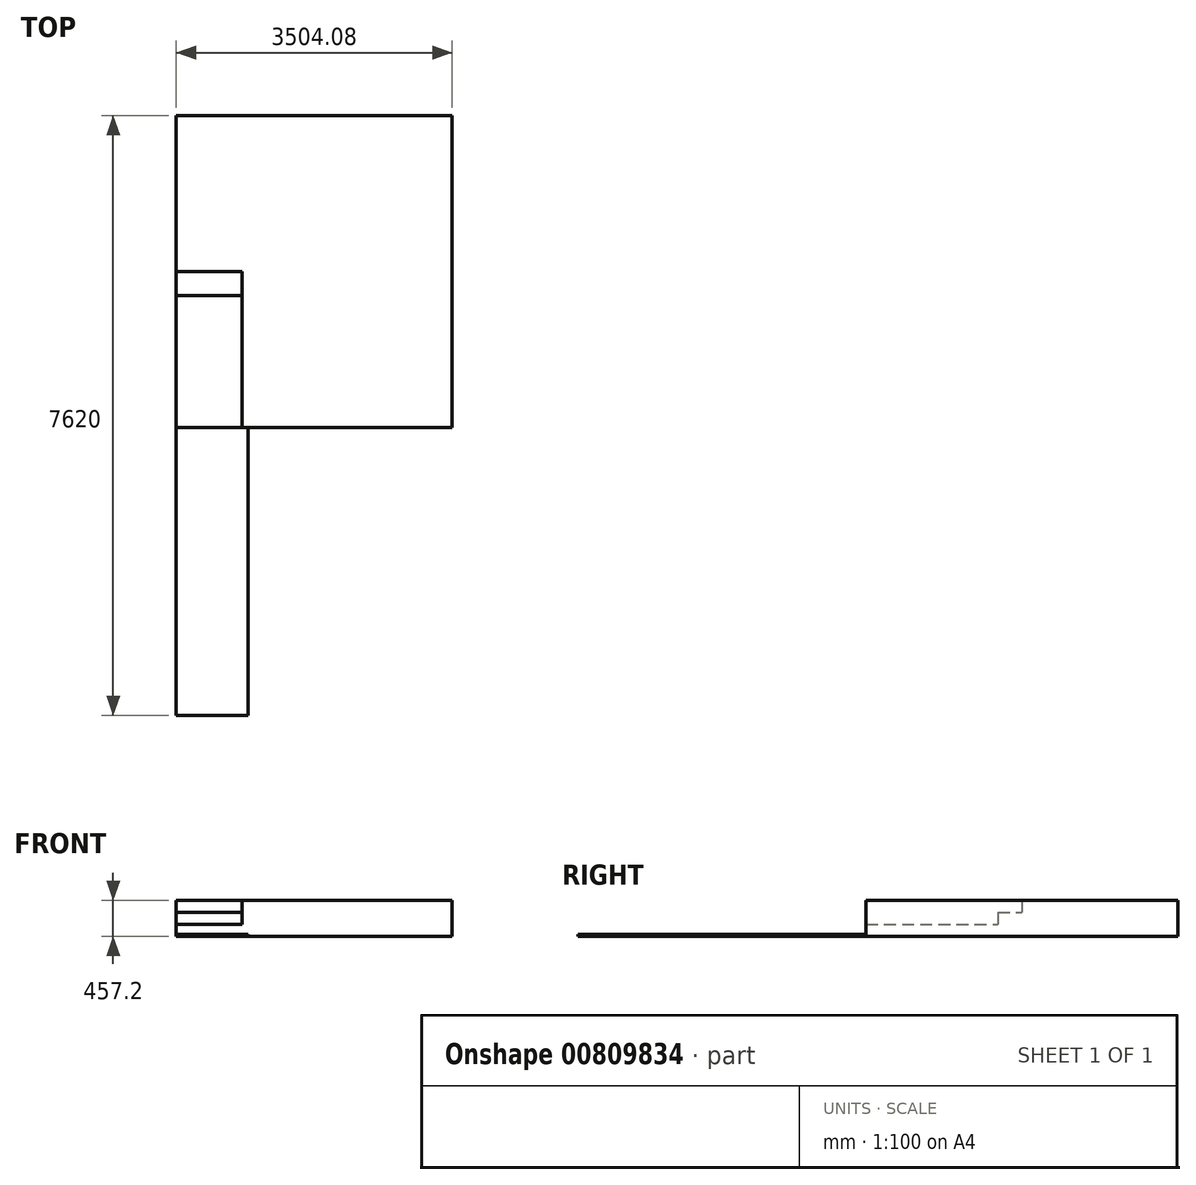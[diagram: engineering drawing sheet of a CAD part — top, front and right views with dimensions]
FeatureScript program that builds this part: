
annotation { "Feature Type Name" : "Feature", "Feature Type Description" : "" }
export const myFeature = defineFeature(function(context is Context, id is Id, definition is map)
    precondition{}
    {
        {
            var Q0;
            Q0=qCreatedBy(makeId("Top.planeOp"),FACE);
            var sketch = newSketch(context, id + "F0", { "sketchPlane" : qUnion([Q0])});
            skLineSegment(sketch, "E0.bottom", {"start": v(1752.04, -1981.2) * mm, "end": v(-1752.04, -1981.2) * mm});
            skLineSegment(sketch, "E0.top", {"start": v(1752.04, 1981.2) * mm, "end": v(-1752.04, 1981.2) * mm});
            skLineSegment(sketch, "E0.left", {"start": v(1752.04, -1981.2) * mm, "end": v(1752.04, 1981.2) * mm});
            skLineSegment(sketch, "E0.right", {"start": v(-1752.04, -1981.2) * mm, "end": v(-1752.04, 1981.2) * mm});
            skPoint(sketch, "E0.middle", {"position": v(0, 0) * mm});
            skLineSegment(sketch, "E1.bottom", {"start": v(-1752.04, -1981.2) * mm, "end": v(-837.64, -1981.2) * mm});
            skLineSegment(sketch, "E1.top", {"start": v(-1752.04, -5638.8) * mm, "end": v(-837.64, -5638.8) * mm});
            skLineSegment(sketch, "E1.left", {"start": v(-1752.04, -1981.2) * mm, "end": v(-1752.04, -5638.8) * mm});
            skLineSegment(sketch, "E1.right", {"start": v(-837.64, -1981.2) * mm, "end": v(-837.64, -5638.8) * mm});
            skLineSegment(sketch, "E2.bottom", {"start": v(-1752.04, -1981.2) * mm, "end": v(-914.4, -1981.2) * mm});
            skLineSegment(sketch, "E2.top", {"start": v(-1752.04, -304.8) * mm, "end": v(-914.4, -304.8) * mm});
            skLineSegment(sketch, "E2.left", {"start": v(-1752.04, -1981.2) * mm, "end": v(-1752.04, -304.8) * mm});
            skLineSegment(sketch, "E2.right", {"start": v(-914.4, -1981.2) * mm, "end": v(-914.4, -304.8) * mm});
            skLineSegment(sketch, "E3.top", {"start": v(-1752.04, 0) * mm, "end": v(-914.4, 0) * mm});
            skLineSegment(sketch, "E3.left", {"start": v(-1752.04, -304.8) * mm, "end": v(-1752.04, 0) * mm});
            skLineSegment(sketch, "E3.right", {"start": v(-914.4, -304.8) * mm, "end": v(-914.4, 0) * mm});
            skSolve(sketch);
        }
        {
            var Q0;
            {var subQ4=sQuery(id+"F0.wireOp",EDGE,"E2.top");Q0=makeQuery(id+"F0.imprint","IMPRINT",FACE,{"disambiguationData":[TD([[makeQuery(id+"F0.imprint","IMPRINT",EDGE,{"derivedFrom":subQ4}),-1.0]])]});}
            extrude(context, id + "F1", {"entities" : qUnion([Q0]), "depth" : 152.4 * mm, "offsetDistance" : 25.4 * mm});
        }
        {
            var Q0;
            {var subQ2=sQuery(id+"F0.wireOp",EDGE,"E2.top");Q0=makeQuery(id+"F0.imprint","IMPRINT",FACE,{"disambiguationData":[TD([[makeQuery(id+"F0.imprint","IMPRINT",EDGE,{"derivedFrom":subQ2}),1.0]])]});}
            extrude(context, id + "F2", {"entities" : qUnion([Q0]), "operationType" : NewBodyOperationType.ADD, "depth" : 304.8 * mm, "offsetDistance" : 25.4 * mm});
        }
        {
            var Q0;
            {var subQ1=sQuery(id+"F0.wireOp",EDGE,"E0.top");Q0=makeQuery(id+"F0.imprint","IMPRINT",FACE,{"disambiguationData":[TD([[makeQuery(id+"F0.imprint","IMPRINT",EDGE,{"derivedFrom":subQ1}),1.0]])]});}
            extrude(context, id + "F3", {"entities" : qUnion([Q0]), "operationType" : NewBodyOperationType.ADD, "depth" : 457.2 * mm, "offsetDistance" : 25.4 * mm});
        }
        {
            var Q0;
            Q0=makeQuery(id+"F0.imprint","IMPRINT",FACE,{"disambiguationData":[TD([[makeQuery(id+"F0.imprint","IMPRINT",EDGE,{"derivedFrom":sQuery(id+"F0.wireOp",EDGE,"E1.top")}),1.0]])]});
            extrude(context, id + "F4", {"entities" : qUnion([Q0]), "operationType" : NewBodyOperationType.ADD, "depth" : 25.4 * mm, "offsetDistance" : 25.4 * mm});
        }
    });
